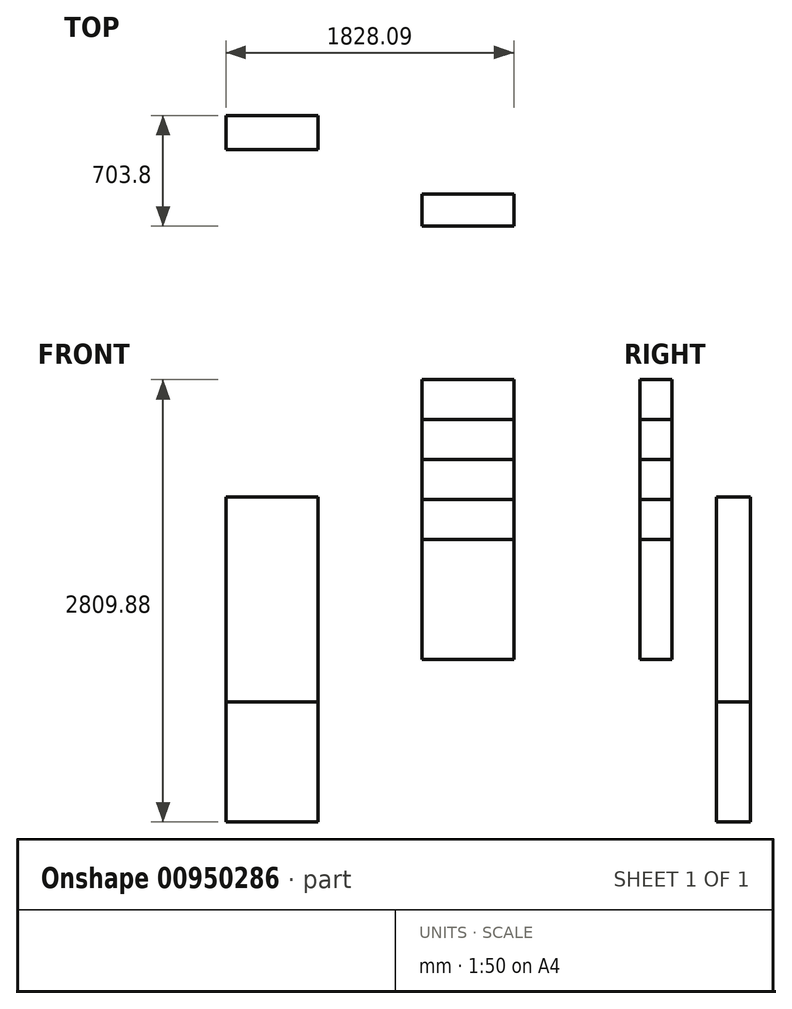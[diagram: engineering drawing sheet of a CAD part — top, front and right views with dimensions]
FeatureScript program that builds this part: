
annotation { "Feature Type Name" : "Feature", "Feature Type Description" : "" }
export const myFeature = defineFeature(function(context is Context, id is Id, definition is map)
    precondition{}
    {
        {
            var Q0;
            Q0=qCreatedBy(makeId("Top.planeOp"),FACE);
            var sketch = newSketch(context, id + "F0", { "sketchPlane" : qUnion([Q0])});
            skLineSegment(sketch, "E0.bottom", {"start": v(292.1, -107.95) * mm, "end": v(-292.1, -107.95) * mm});
            skLineSegment(sketch, "E0.top", {"start": v(292.1, 107.95) * mm, "end": v(-292.1, 107.95) * mm});
            skLineSegment(sketch, "E0.left", {"start": v(292.1, -107.95) * mm, "end": v(292.1, 107.95) * mm});
            skLineSegment(sketch, "E0.right", {"start": v(-292.1, -107.95) * mm, "end": v(-292.1, 107.95) * mm});
            skPoint(sketch, "E0.middle", {"position": v(0, 0) * mm});
            skSolve(sketch);
        }
        {
            var Q0;
            Q0=qCreatedBy(makeId("Top.planeOp"),FACE);
            var sketch = newSketch(context, id + "F1", { "sketchPlane" : qUnion([Q0])});
            skLineSegment(sketch, "E1.bottom", {"start": v(618.88, 5.61) * mm, "end": v(1203.08, 5.61) * mm});
            skLineSegment(sketch, "E1.top", {"start": v(618.88, -210.29) * mm, "end": v(1203.08, -210.29) * mm});
            skLineSegment(sketch, "E1.left", {"start": v(618.88, 5.61) * mm, "end": v(618.88, -210.29) * mm});
            skLineSegment(sketch, "E1.right", {"start": v(1203.08, 5.61) * mm, "end": v(1203.08, -210.29) * mm});
            skSolve(sketch);
        }
        {
            var Q0;
            Q0 = qSketchRegion(id + "F1", true);
            extrude(context, id + "F2", {"entities" : qUnion([Q0]), "endBound" : BoundingType.SYMMETRIC, "depth" : 2063.75 * mm, "offsetDistance" : 25.4 * mm});
        }
        {
            var Q0;
            Q0=makeQuery(id+"F2.opExtrude","CAP_FACE",FACE,{"disambiguationData":[OSD([sQuery(id+"F1.wireOp",EDGE,"E1.bottom"),sQuery(id+"F1.wireOp",EDGE,"E1.top"),sQuery(id+"F1.wireOp",EDGE,"E1.left"),sQuery(id+"F1.wireOp",EDGE,"E1.right")])],"isStart":true});
            var sketch = newSketch(context, id + "F3", { "sketchPlane" : qUnion([Q0])});
            skLineSegment(sketch, "E2.bottom", {"start": v(618.88, -5.61) * mm, "end": v(1203.08, -5.61) * mm});
            skLineSegment(sketch, "E2.top", {"start": v(618.88, 210.29) * mm, "end": v(1203.08, 210.29) * mm});
            skLineSegment(sketch, "E2.left", {"start": v(618.88, -5.61) * mm, "end": v(618.88, 210.29) * mm});
            skLineSegment(sketch, "E2.right", {"start": v(1203.08, -5.61) * mm, "end": v(1203.08, 210.29) * mm});
            skSolve(sketch);
        }
        {
            var Q0;
            Q0 = qSketchRegion(id + "F3", true);
            extrude(context, id + "F4", {"entities" : qUnion([Q0]), "oppositeDirection" : true, "depth" : 762 * mm, "offsetDistance" : 25.4 * mm});
        }
        {
            var Q0;
            Q0=makeQuery(id+"F0.imprint","IMPRINT",FACE,{"disambiguationData":[TD([[makeQuery(id+"F0.imprint","IMPRINT",EDGE,{"derivedFrom":sQuery(id+"F0.wireOp",EDGE,"E0.bottom")}),-1.0]])]});
            var sketch = newSketch(context, id + "F5", { "sketchPlane" : qUnion([Q0])});
            skLineSegment(sketch, "E3.bottom", {"start": v(1862.77, -494.99) * mm, "end": v(2446.97, -494.99) * mm});
            skLineSegment(sketch, "E3.top", {"start": v(1862.77, -698.19) * mm, "end": v(2446.97, -698.19) * mm});
            skLineSegment(sketch, "E3.left", {"start": v(1862.77, -494.99) * mm, "end": v(1862.77, -698.19) * mm});
            skLineSegment(sketch, "E3.right", {"start": v(2446.97, -494.99) * mm, "end": v(2446.97, -698.19) * mm});
            skSolve(sketch);
        }
        {
            var Q0;
            Q0 = qSketchRegion(id + "F5", true);
            extrude(context, id + "F6", {"entities" : qUnion([Q0]), "depth" : 762 * mm, "offsetDistance" : 25.4 * mm});
        }
        {
            var Q0;
            Q0=makeQuery(id+"F6.opExtrude","CAP_FACE",FACE,{"disambiguationData":[OSD([sQuery(id+"F5.wireOp",EDGE,"E3.bottom"),sQuery(id+"F5.wireOp",EDGE,"E3.top"),sQuery(id+"F5.wireOp",EDGE,"E3.left"),sQuery(id+"F5.wireOp",EDGE,"E3.right")])],"isStart":false});
            extrude(context, id + "F7", {"entities" : qUnion([Q0]), "depth" : 254 * mm, "offsetDistance" : 25.4 * mm});
        }
        {
            var Q0;
            Q0=makeQuery(id+"F7.opExtrude","CAP_FACE",FACE,{"disambiguationData":[OSD([sQuery(id+"F5.wireOp",EDGE,"E3.bottom"),sQuery(id+"F5.wireOp",EDGE,"E3.top"),sQuery(id+"F5.wireOp",EDGE,"E3.left"),sQuery(id+"F5.wireOp",EDGE,"E3.right")])],"isStart":false});
            extrude(context, id + "F8", {"entities" : qUnion([Q0]), "depth" : 254 * mm, "offsetDistance" : 25.4 * mm});
        }
        {
            var Q0;
            Q0=makeQuery(id+"F8.opExtrude","CAP_FACE",FACE,{"disambiguationData":[OSD([sQuery(id+"F5.wireOp",EDGE,"E3.bottom"),sQuery(id+"F5.wireOp",EDGE,"E3.top"),sQuery(id+"F5.wireOp",EDGE,"E3.left"),sQuery(id+"F5.wireOp",EDGE,"E3.right")])],"isStart":false});
            extrude(context, id + "F9", {"entities" : qUnion([Q0]), "depth" : 254 * mm, "offsetDistance" : 25.4 * mm});
        }
        {
            var Q0;
            Q0=makeQuery(id+"F9.opExtrude","CAP_FACE",FACE,{"disambiguationData":[OSD([sQuery(id+"F5.wireOp",EDGE,"E3.bottom"),sQuery(id+"F5.wireOp",EDGE,"E3.top"),sQuery(id+"F5.wireOp",EDGE,"E3.left"),sQuery(id+"F5.wireOp",EDGE,"E3.right")])],"isStart":false});
            extrude(context, id + "F10", {"entities" : qUnion([Q0]), "depth" : 254 * mm, "offsetDistance" : 25.4 * mm});
        }
    });
